# Revit family: Tank-System_In-Wall_Dual-Flush_WT152M_TOTO
name_source: partatom
category: Plumbing Fixtures
revit_build: Autodesk Revit Architecture 2013 (Build: 20130531_2115(x64)
units: mm (PartAtom-declared; Revit-internal decimal feet)

## types (1)
- WT152M
    04 CSI = 22 42 13
    95 CSI = 15410-800
    ADA Compliant = No
    Assembly Code = D2010110
    Bowl Material = Various
    CAD Drawing URL = http://assets.totousa.com
    CWFU = 0
    Certifications = IAPMO (cUPC), State of Massachusetts, City of Los Angeles, and others
    Code Compliance = UPC, IPC, NSPC, NPC Canada, and others
    Cold Water Connection NPT Radius = 1/4"
    Cost = 0 $
    Description = In-Wall Tank System, 1.6GPF & 0.9GPF
    Flush System = Dual-Max
    Gallons Per Flush = 1.60 gal
    HW Connection = No
    HWFU = 0
    Height = 44 1/2"
    Height Range = Adjustable 3' - 8 1/2" to 4' - 4"
    Industry Standards = Meets and exceeds ASME A112.19.2/CSA B45.1
    Inlet Drain Hole Height = 12"
    Inlet Drain Hole Inner Radius = 3/4"
    Inlet Drain Hole Radius = 1"
    Length = 25 1/8"
    Manufacturer = TOTO USA, Inc.
    Manufacturer Fax = (770) 282-0002
    Material = Vitreous China
    Model = WT152M
    Mount Type = Wall
    Outlet Drain Hole Height = 8"
    Outlet Drain Hole Inner Radius = 1 1/4"
    Outlet Drain Hole Radius = 1 1/2"
    Push Plate Hole Height = 30"
    SanoGloss Available = No
    Shipping Weight = 38.00 lb
    Spec Sheet URL = http://assets.totousa.com
    Subcategory = Toilets
    Toto BIM Number = BM-00350
    URL = http://www.totousa.com
    Vent Connection = Yes
    WFU = 0
    Warranty = One Year Limited Warranty
    Warranty URL = http://www.totousa.com
    Waste Connection = Yes
    Waste Connection NPT Radius = 1"
    Water Closet Material = Vitreous China
    WaterSense = No
    Width = 38"

## geometry (parser evidence)
native form markers: Blend x18, Sweep x4
no freeform markers — native parametric forms only
